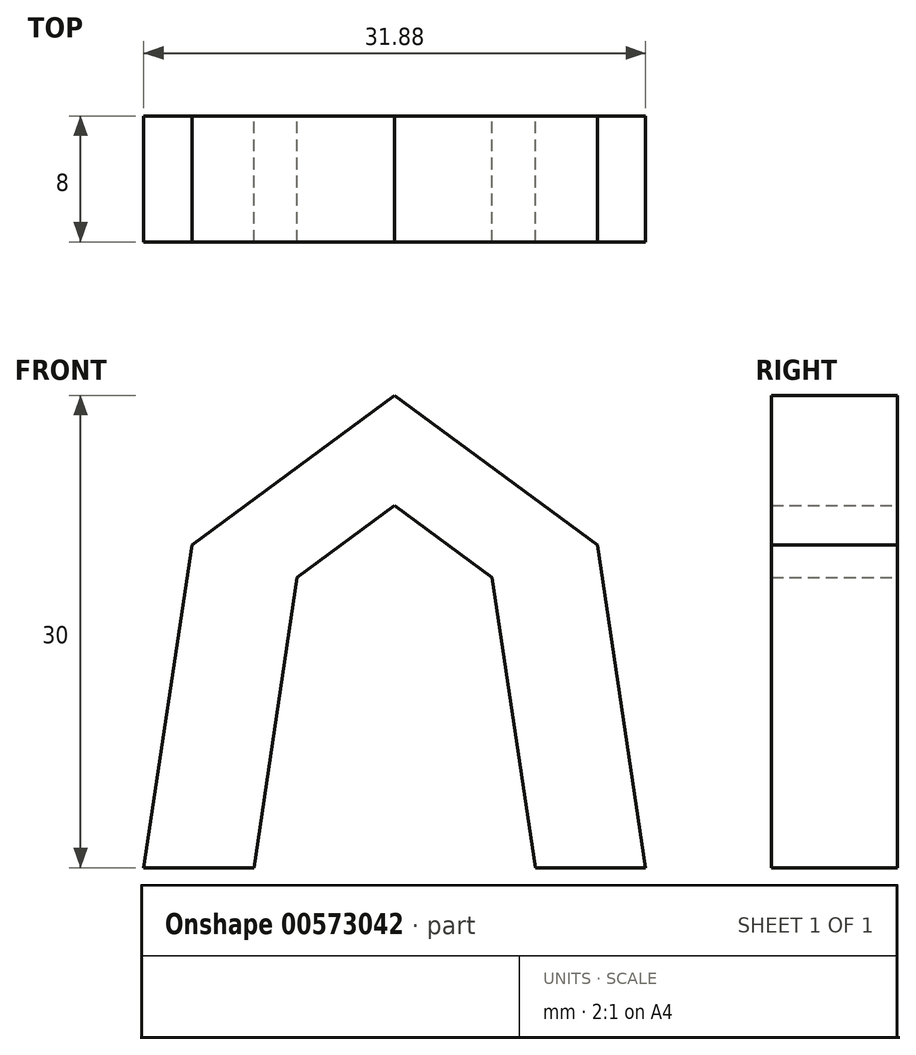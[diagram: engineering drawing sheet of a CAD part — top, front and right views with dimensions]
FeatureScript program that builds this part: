
annotation { "Feature Type Name" : "Feature", "Feature Type Description" : "" }
export const myFeature = defineFeature(function(context is Context, id is Id, definition is map)
    precondition{}
    {
        {
            var Q0;
            Q0=qCreatedBy(makeId("Front.planeOp"),FACE);
            var sketch = newSketch(context, id + "F0", { "sketchPlane" : qUnion([Q0])});
            skLineSegment(sketch, "E0", {"start": v(-19.5, 30.45) * mm, "end": v(-19.5, -47.1) * mm, "construction": true});
            skLineSegment(sketch, "E1", {"start": v(-18.5, 34.89) * mm, "end": v(-18.5, -18.54) * mm, "construction": true});
            skLineSegment(sketch, "E2", {"start": v(-19.5, 13.67) * mm, "end": v(0, 13.67) * mm});
            skLineSegment(sketch, "E3", {"start": v(-18.5, 5.45) * mm, "end": v(0, 5.45) * mm});
            skLineSegment(sketch, "E4", {"start": v(-19.5, 13.67) * mm, "end": v(-19.26, 11.67) * mm});
            skLineSegment(sketch, "E5", {"start": v(-19.26, 11.67) * mm, "end": v(0, 11.67) * mm, "construction": true});
            skLineSegment(sketch, "E6", {"start": v(-19.01, 9.67) * mm, "end": v(0, 9.67) * mm, "construction": true});
            skLineSegment(sketch, "E7", {"start": v(-18.93, 10.67) * mm, "end": v(-13.02, 10.67) * mm, "construction": true});
            skArc(sketch, "E8", {"start": v(-19.26, 11.67) * mm, "mid": v(-18.14, 10.79) * mm, "end": v(-19.01, 9.67) * mm});
            skLineSegment(sketch, "E9.trimOffspring", {"start": v(-19.01, 9.67) * mm, "end": v(-18.5, 5.45) * mm});
            skLineSegment(sketch, "E10", {"start": v(0, 15.55) * mm, "end": v(0, 2.56) * mm, "construction": true});
            skLineSegment(sketch, "E11", {"start": v(2.58, 43.67) * mm, "end": v(-26.14, 43.67) * mm, "construction": true});
            skLineSegment(sketch, "E12", {"start": v(-15.94, 13.67) * mm, "end": v(-12.88, 34.18) * mm});
            skLineSegment(sketch, "E13", {"start": v(-12.88, 34.18) * mm, "end": v(0, 43.67) * mm});
            skLineSegment(sketch, "E14", {"start": v(-8.94, 13.67) * mm, "end": v(-6.19, 32.1) * mm});
            skLineSegment(sketch, "E15", {"start": v(-6.19, 32.1) * mm, "end": v(0, 36.67) * mm});
            skLineSegment(sketch, "E16.MirrorCS", {"start": v(12.88, 34.18) * mm, "end": v(0, 43.67) * mm});
            skLineSegment(sketch, "E17.MirrorCS", {"start": v(15.94, 13.67) * mm, "end": v(12.88, 34.18) * mm});
            skLineSegment(sketch, "E18.MirrorCS", {"start": v(6.19, 32.1) * mm, "end": v(0, 36.67) * mm});
            skLineSegment(sketch, "E19.MirrorCS", {"start": v(8.94, 13.67) * mm, "end": v(6.19, 32.1) * mm});
            skLineSegment(sketch, "E20", {"start": v(8.94, 13.67) * mm, "end": v(15.94, 13.67) * mm});
            skSolve(sketch);
        }
        {
            var Q0;
            Q0=sQuery(id+"F0.wireOp",EDGE,"E2");
            var Q1;
            Q1=sQuery(id+"F0.wireOp",EDGE,"E4");
            var Q2;
            Q2=sQuery(id+"F0.wireOp",EDGE,"E8");
            var Q3;
            Q3=sQuery(id+"F0.wireOp",EDGE,"E9.trimOffspring");
            var Q4;
            Q4=sQuery(id+"F0.wireOp",EDGE,"E3");
            var Q5;
            Q5=sQuery(id+"F0.wireOp",EDGE,"E10");
            revolve(context, id + "F1", {"bodyType" : ToolBodyType.SURFACE, "surfaceEntities" : qUnion([Q0, Q1, Q2, Q3, Q4]), "axis" : qUnion([Q5]), "revolveType" : RevolveType.FULL, "surfaceOperationType" : NewSurfaceOperationType.NEW});
        }
        {
            var Q0;
            {var subQ1=sQuery(id+"F0.wireOp",EDGE,"E12");Q0=makeQuery(id+"F0.imprint","IMPRINT",FACE,{"disambiguationData":[TD([[makeQuery(id+"F0.imprint","IMPRINT",EDGE,{"derivedFrom":subQ1}),-1.0]])]});}
            extrude(context, id + "F2", {"entities" : qUnion([Q0]), "depth" : 8 * mm, "offsetDistance" : 25 * mm, "symmetric" : true});
        }
    });
